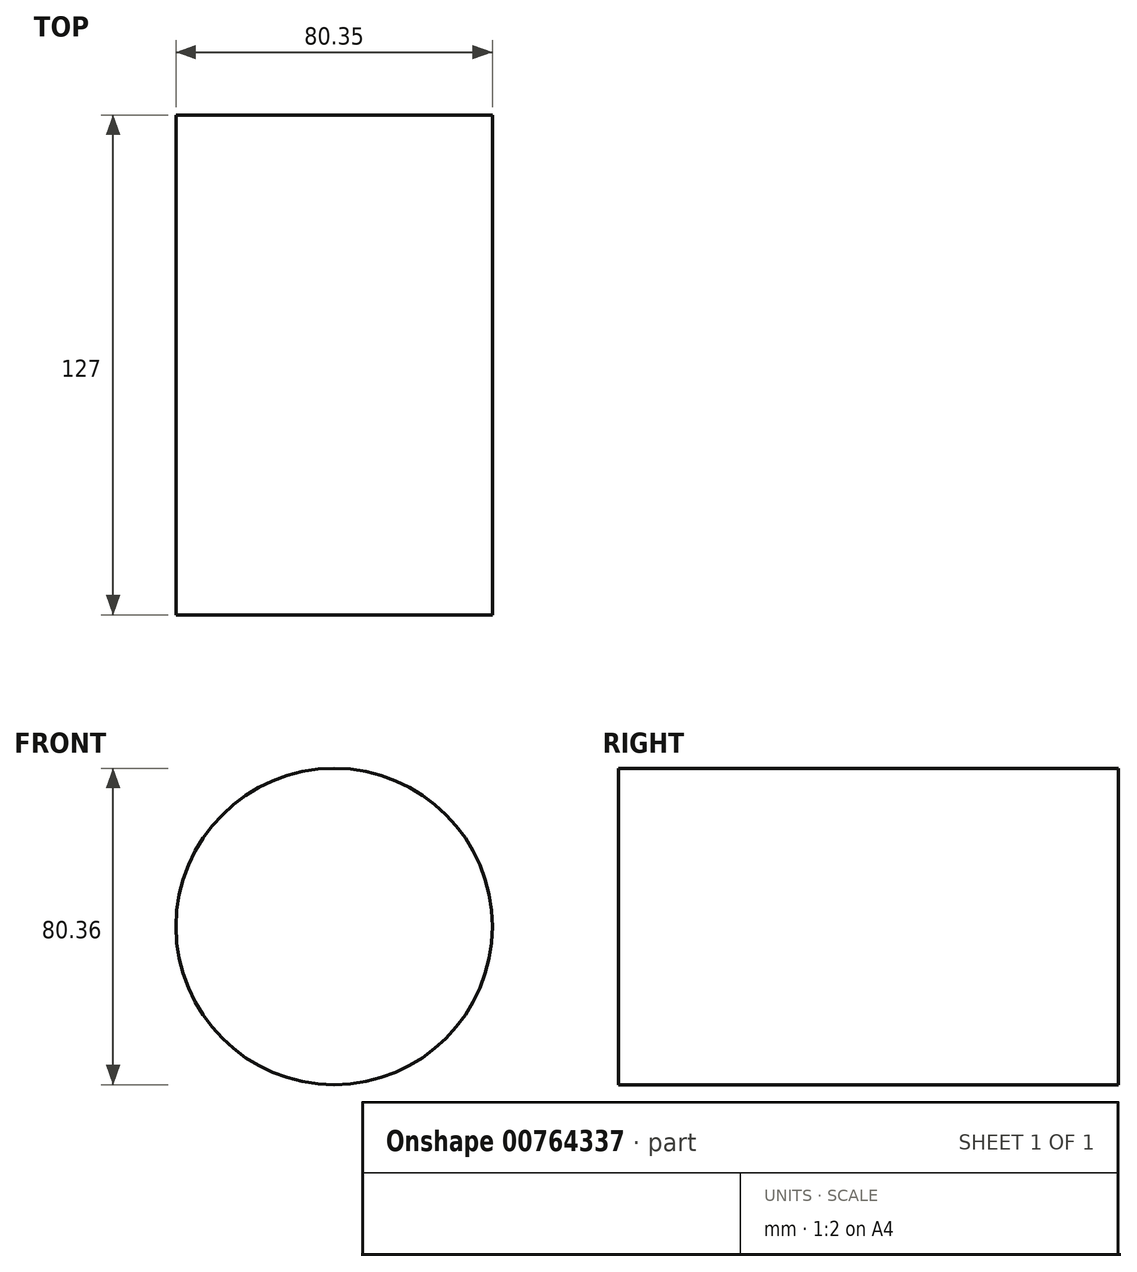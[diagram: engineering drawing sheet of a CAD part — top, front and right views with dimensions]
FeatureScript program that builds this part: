
annotation { "Feature Type Name" : "Feature", "Feature Type Description" : "" }
export const myFeature = defineFeature(function(context is Context, id is Id, definition is map)
    precondition{}
    {
        {
            var Q0;
            Q0=qCreatedBy(makeId("Front.planeOp"),FACE);
            var sketch = newSketch(context, id + "F0", { "sketchPlane" : qUnion([Q0])});
            skCircle(sketch, "E0", {"center": v(-19.98, 11.75) * mm, "radius": 40.18 * mm});
            skSolve(sketch);
        }
        {
            var Q0;
            Q0=makeQuery(id+"F0.imprint","IMPRINT",FACE,{"disambiguationData":[TD([[makeQuery(id+"F0.imprint","IMPRINT",EDGE,{"derivedFrom":sQuery(id+"F0.wireOp",EDGE,"E0")}),1.0]])]});
            extrude(context, id + "F1", {"entities" : qUnion([Q0]), "depth" : 127 * mm, "offsetDistance" : 25.4 * mm});
        }
    });
